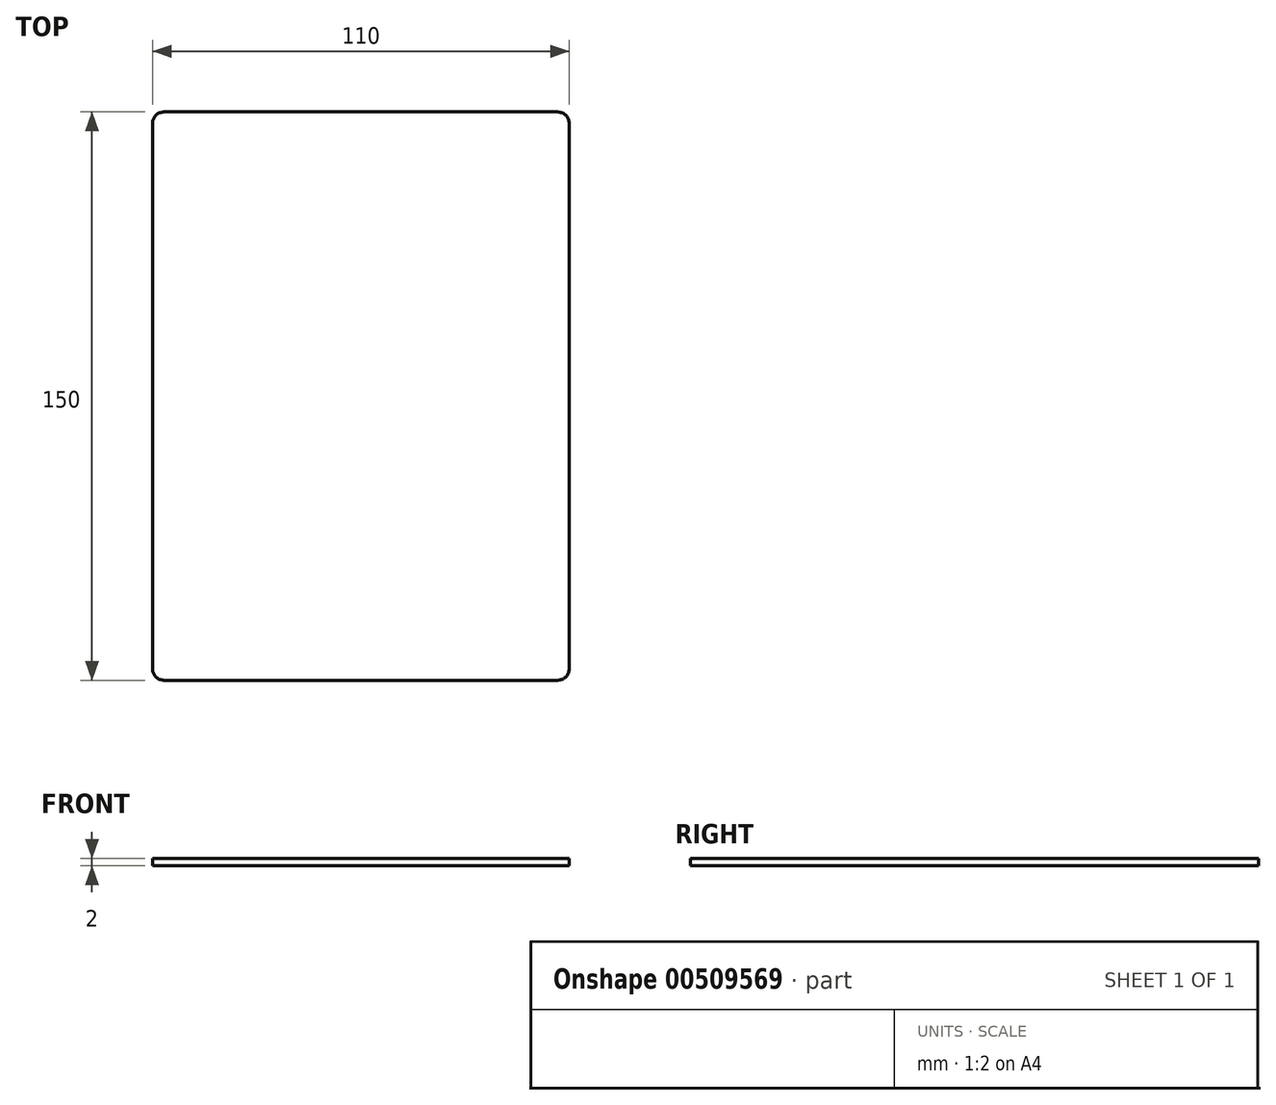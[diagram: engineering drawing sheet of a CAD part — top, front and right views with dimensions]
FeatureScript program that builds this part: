
annotation { "Feature Type Name" : "Feature", "Feature Type Description" : "" }
export const myFeature = defineFeature(function(context is Context, id is Id, definition is map)
    precondition{}
    {
        {
            var Q0;
            Q0=qCreatedBy(makeId("Top.planeOp"),FACE);
            var sketch = newSketch(context, id + "F0", { "sketchPlane" : qUnion([Q0])});
            skLineSegment(sketch, "E0.bottom", {"start": v(-50.67, 126.94) * mm, "end": v(59.33, 126.94) * mm});
            skLineSegment(sketch, "E0.top", {"start": v(-50.67, -23.06) * mm, "end": v(59.33, -23.06) * mm});
            skLineSegment(sketch, "E0.left", {"start": v(-50.67, 126.94) * mm, "end": v(-50.67, -23.06) * mm});
            skLineSegment(sketch, "E0.right", {"start": v(59.33, 126.94) * mm, "end": v(59.33, -23.06) * mm});
            skSolve(sketch);
        }
        {
            var Q0;
            Q0=makeQuery(id+"F0.imprint","IMPRINT",FACE,{"disambiguationData":[TD([[makeQuery(id+"F0.imprint","IMPRINT",EDGE,{"derivedFrom":sQuery(id+"F0.wireOp",EDGE,"E0.bottom")}),-1.0]])]});
            extrude(context, id + "F1", {"entities" : qUnion([Q0]), "depth" : 2 * mm});
        }
        {
            var Q0;
            Q0=makeQuery(id+"F1.opExtrude","SWEPT_EDGE",EDGE,{"disambiguationData":[OSD([sQuery(id+"F0.wireOp",EDGE,"E0.bottom"),sQuery(id+"F0.wireOp",EDGE,"E0.left")])]});
            var Q1;
            Q1=makeQuery(id+"F1.opExtrude","SWEPT_EDGE",EDGE,{"disambiguationData":[OSD([sQuery(id+"F0.wireOp",EDGE,"E0.top"),sQuery(id+"F0.wireOp",EDGE,"E0.left")])]});
            var Q2;
            Q2=makeQuery(id+"F1.opExtrude","SWEPT_EDGE",EDGE,{"disambiguationData":[OSD([sQuery(id+"F0.wireOp",EDGE,"E0.top"),sQuery(id+"F0.wireOp",EDGE,"E0.right")])]});
            var Q3;
            Q3=makeQuery(id+"F1.opExtrude","SWEPT_EDGE",EDGE,{"disambiguationData":[OSD([sQuery(id+"F0.wireOp",EDGE,"E0.bottom"),sQuery(id+"F0.wireOp",EDGE,"E0.right")])]});
            fillet(context, id + "F2", {"entities" : qUnion([Q0, Q1, Q2, Q3]), "radius" : 3 * mm, "tangentPropagation" : true, "allowEdgeOverflow" : false});
        }
    });
